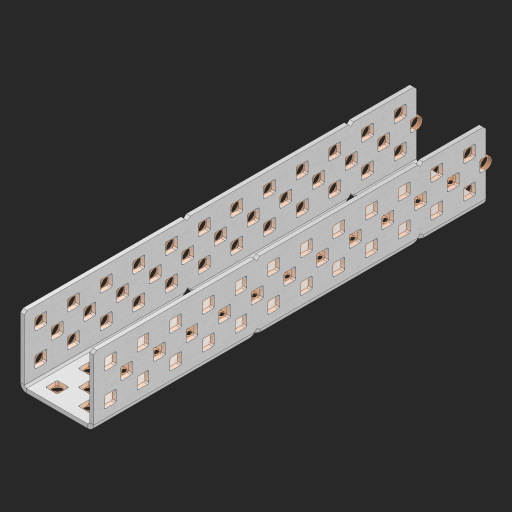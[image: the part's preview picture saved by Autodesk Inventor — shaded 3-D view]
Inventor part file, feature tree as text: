
AUTODESK INVENTOR PART (.ipt)
format: ipt  version: 2023 (Build 270158000, 158)  size: 1,510,912 bytes
history: native  units: in
note: dims shown in document units (in); Inventor stores cm internally (conversion verified against a paired STEP export)
features: other x150, extrude x142, sheet_metal_op x8, sketch x7, mirror x3, pattern_linear x2, chamfer x1
ambient origin geometry x8: Origin, YZ Plane, XZ Plane, XY Plane, X Axis, Y Axis, Z Axis, Center Point
bodies: Solid1 (feature_tree), Body (feature_tree)
feature tree (313):
  sheet_metal_op  "Flanges"
  sheet_metal_op  "Body Pattern"
  pattern_linear  "Center Pattern"  Spacing1=1.0in  [1 undecoded]
  other  "Arc Length"
  mirror  "Notch Mirror"
  pattern_linear  "Notch Pattern"  Spacing1=0.25in  [1 undecoded]
  other  "Diagonal Plane"
  mirror  "Flange 1"
  mirror  "Flange 2"
  chamfer  "End Chamfer"
  sketch  "Sketch1"  dims[d0=1.0in]
  other  "Plate1"
  sketch  "Sketch2"  dims[d1=6.0in]
  other  "Plate2"
  sheet_metal_op  "Bend1"
  sheet_metal_op  "Corner1"
  sketch  "Sketch8"  dims[d2=0.0625in]
  sketch  "Sketch9"  dims[d3=0.0625in]
  other  "Srf91"
  sheet_metal_op  "Body Pattern Sketch"
  other  "Srf92"
  sketch  "Sketch13"  dims[d4=0.0312in]
  sketch  "Sketch15"  dims[d5=0.125in]
  sketch  "Sketch16"  dims[d6=0.0625in d7=1.0in d8=90.0deg d9=0.0312in d10=0.25in d11=0.0625in d12=0.0625in d49=0.182in d50=0.02in d52=0.25in d53=0.0625in d54=0.0in d55=0.172in d56=1.0in d57=0.0in d60=4.7244in d62=0.5in d63=0.7874in d65=0.5in d85=0.1473in d86=0.1782in d88=0.04in d89=0.0625in d90=0.0in d91=0.04in d92=0.0491in d95=2.5in d96=0.04in d97=0.25in d98=45.0deg d99=0.25in d102=2.497in d106=0.182in d107=0.02in d108=0.5in d110=0.0625in d111=0.0in d112=0.172in d113=0.5in d114=0.0in d117=0.5in d118=0.5in d131=0.25in d132=0.25in]
  other  "Srf786"
  other  "Srf889"
  other  "Srf890"
  other  "Srf891"
  other  "Srf892"
  other  "Srf893"
  other  "Srf894"
  other  "Srf895"
  other  "Srf896"
  other  "Srf996"
  other  "Srf997"
  other  "Srf998"
  other  "Srf1315"
  other  "Srf1316"
  other  "Srf1317"
  other  "Srf1325"
  other  "Srf1326"
  other  "Srf1327"
  other  "Srf1328"
  other  "Srf1329"
  other  "Srf1330"
  other  "Srf1331"
  other  "Srf1332"
  other  "Srf1338"
  other  "Srf1339"
  other  "Srf1340"
  other  "Srf1374"
  other  "Srf1375"
  other  "Srf1376"
  other  "Srf1384"
  other  "Srf1385"
  other  "Srf1386"
  other  "Srf1387"
  other  "Srf1388"
  other  "Srf1389"
  other  "Srf1390"
  other  "Srf1391"
  other  "Srf1397"
  other  "Srf1398"
  other  "Srf1399"
  other  "Srf1433"
  other  "Srf1434"
  other  "Srf1473"
  other  "Srf1474"
  other  "Srf1475"
  other  "Srf1476"
  other  "Srf1477"
  other  "Srf1478"
  other  "Srf1479"
  other  "Srf1480"
  other  "Srf1481"
  other  "Srf1482"
  other  "Srf1483"
  other  "Srf1484"
  other  "Srf1500"
  other  "Srf1501"
  other  "Srf1502"
  other  "Srf1503"
  other  "Srf1504"
  other  "Srf1505"
  other  "Srf1506"
  other  "Srf1507"
  other  "Srf1508"
  other  "Srf1509"
  other  "Srf1510"
  other  "Srf1511"
  other  "Srf1512"
  other  "Srf1513"
  other  "Srf1514"
  other  "Srf1515"
  other  "Srf1516"
  other  "Srf1517"
  other  "Srf1518"
  other  "Srf1519"
  other  "Srf1520"
  other  "Srf1521"
  other  "Srf1538"
  other  "Srf1539"
  other  "Srf1540"
  other  "Srf1541"
  other  "Srf1542"
  other  "Srf1543"
  other  "Srf1544"
  other  "Srf1545"
  other  "Srf1546"
  other  "Srf1547"
  other  "Srf1548"
  other  "Srf1549"
  other  "Srf1550"
  other  "Srf1551"
  other  "Srf1552"
  other  "Srf1553"
  other  "Srf1554"
  other  "Srf1555"
  other  "Srf1556"
  other  "Srf1557"
  other  "Srf1558"
  other  "Srf1559"
  other  "Srf1576"
  other  "Srf1577"
  other  "Srf1578"
  other  "Srf1579"
  other  "Srf1580"
  other  "Srf1581"
  other  "Srf1582"
  other  "Srf1583"
  other  "Srf1584"
  other  "Srf1585"
  other  "Srf1586"
  other  "Srf1587"
  other  "Srf1588"
  other  "Srf1589"
  other  "Srf1590"
  other  "Srf1591"
  other  "Srf1592"
  other  "Srf1593"
  other  "Srf1594"
  other  "Srf1595"
  other  "Srf1596"
  other  "Srf1597"
  other  "Srf1614"
  other  "Srf1615"
  other  "Srf1616"
  other  "Srf1617"
  other  "Srf1618"
  other  "Srf1619"
  other  "Srf1620"
  other  "Srf1621"
  other  "Srf1622"
  other  "Srf1623"
  other  "Srf1624"
  other  "Srf1625"
  other  "Srf1626"
  other  "Srf1627"
  other  "Srf1628"
  other  "Srf1629"
  other  "Srf1630"
  other  "Srf1631"
  other  "Srf1632"
  other  "Srf1633"
  other  "Srf1634"
  other  "Srf1635"
  sheet_metal_op  "Body Stamp"
  sheet_metal_op  "Body Circle"
  other  "Center Stamp"
  other  "Center Circle"
  sheet_metal_op  "Notch"
  extrude  "ExtrusionSrf92"  Depth=0.0625in
  extrude  "ExtrusionSrf889"  Depth=0.0625in
  extrude  "ExtrusionSrf890"  Depth=0.182in
  extrude  "ExtrusionSrf891"  Depth=0.02in
  extrude  "ExtrusionSrf892"  Depth=0.25in
  extrude  "ExtrusionSrf893"  Depth=0.0625in
  extrude  "ExtrusionSrf894"  TaperAngle=0.0deg  [1 undecoded]
  extrude  "ExtrusionSrf895"  Depth=0.25in
  extrude  "ExtrusionSrf896"  Depth=1.0in TaperAngle=0.0deg
  extrude  "ExtrusionSrf996"  Depth=0.25in
  extrude  "ExtrusionSrf997"  Depth=0.5in
  extrude  "ExtrusionSrf998"  Depth=0.25in
  extrude  "ExtrusionSrf1315"  Depth=0.25in
  extrude  "ExtrusionSrf1316"  Depth=0.25in
  extrude  "ExtrusionSrf1355"  Depth=0.0625in
  extrude  "ExtrusionSrf1356"  TaperAngle=0.0deg  [1 undecoded]
  extrude  "ExtrusionSrf1357"  Depth=0.25in
  extrude  "ExtrusionSrf1358"  Depth=0.25in
  extrude  "ExtrusionSrf1359"  Depth=2.5in
  extrude  "ExtrusionSrf1360"  Depth=0.25in TaperAngle=45.0deg
  extrude  "ExtrusionSrf1361"  Depth=0.25in
  extrude  "ExtrusionSrf1362"  Depth=0.25in
  extrude  "ExtrusionSrf1363"  Depth=0.182in
  extrude  "ExtrusionSrf1364"  Depth=0.02in
  extrude  "ExtrusionSrf1365"  Depth=0.5in
  extrude  "ExtrusionSrf1366"  Depth=0.0625in
  extrude  "ExtrusionSrf1374"  TaperAngle=0.0deg  [1 undecoded]
  extrude  "ExtrusionSrf1375"  Depth=0.25in
  extrude  "ExtrusionSrf1414"  Depth=0.5in TaperAngle=0.0deg
  extrude  "ExtrusionSrf1415"  Depth=0.5in
  extrude  "ExtrusionSrf1416"  Depth=0.5in
  extrude  "ExtrusionSrf1417"  Depth=0.25in
  extrude  "ExtrusionSrf1418"  Depth=0.25in
  extrude  "ExtrusionSrf1419"  [1 undecoded]
  extrude  "ExtrusionSrf1420"  [1 undecoded]
  extrude  "ExtrusionSrf1421"  [1 undecoded]
  extrude  "ExtrusionSrf1422"  [1 undecoded]
  extrude  "ExtrusionSrf1423"  [1 undecoded]
  extrude  "ExtrusionSrf1424"  [1 undecoded]
  extrude  "ExtrusionSrf1425"  [1 undecoded]
  extrude  "ExtrusionSrf1433"  [1 undecoded]
  extrude  "ExtrusionSrf1434"  [1 undecoded]
  extrude  "ExtrusionSrf1473"  [1 undecoded]
  extrude  "ExtrusionSrf1474"  [1 undecoded]
  extrude  "ExtrusionSrf1475"  [1 undecoded]
  extrude  "ExtrusionSrf1476"  [1 undecoded]
  extrude  "ExtrusionSrf1477"  [1 undecoded]
  extrude  "ExtrusionSrf1478"  [1 undecoded]
  extrude  "ExtrusionSrf1479"  [1 undecoded]
  extrude  "ExtrusionSrf1480"  [1 undecoded]
  extrude  "ExtrusionSrf1481"  [1 undecoded]
  extrude  "ExtrusionSrf1482"  [1 undecoded]
  extrude  "ExtrusionSrf1483"  [1 undecoded]
  extrude  "ExtrusionSrf1484"  [1 undecoded]
  extrude  "ExtrusionSrf1500"  [1 undecoded]
  extrude  "ExtrusionSrf1501"  [1 undecoded]
  extrude  "ExtrusionSrf1502"  [1 undecoded]
  extrude  "ExtrusionSrf1503"  [1 undecoded]
  extrude  "ExtrusionSrf1504"  [1 undecoded]
  extrude  "ExtrusionSrf1505"  [1 undecoded]
  extrude  "ExtrusionSrf1506"  [1 undecoded]
  extrude  "ExtrusionSrf1507"  [1 undecoded]
  extrude  "ExtrusionSrf1508"  [1 undecoded]
  extrude  "ExtrusionSrf1509"  [1 undecoded]
  extrude  "ExtrusionSrf1510"  [1 undecoded]
  extrude  "ExtrusionSrf1511"  [1 undecoded]
  extrude  "ExtrusionSrf1512"  [1 undecoded]
  extrude  "ExtrusionSrf1513"  [1 undecoded]
  extrude  "ExtrusionSrf1514"  [1 undecoded]
  extrude  "ExtrusionSrf1515"  [1 undecoded]
  extrude  "ExtrusionSrf1516"  [1 undecoded]
  extrude  "ExtrusionSrf1517"  [1 undecoded]
  extrude  "ExtrusionSrf1518"  [1 undecoded]
  extrude  "ExtrusionSrf1519"  [1 undecoded]
  extrude  "ExtrusionSrf1520"  [1 undecoded]
  extrude  "ExtrusionSrf1521"  [1 undecoded]
  extrude  "ExtrusionSrf1538"  [1 undecoded]
  extrude  "ExtrusionSrf1539"  [1 undecoded]
  extrude  "ExtrusionSrf1540"  [1 undecoded]
  extrude  "ExtrusionSrf1541"  [1 undecoded]
  extrude  "ExtrusionSrf1542"  [1 undecoded]
  extrude  "ExtrusionSrf1543"  [1 undecoded]
  extrude  "ExtrusionSrf1544"  [1 undecoded]
  extrude  "ExtrusionSrf1545"  [1 undecoded]
  extrude  "ExtrusionSrf1546"  [1 undecoded]
  extrude  "ExtrusionSrf1547"  [1 undecoded]
  extrude  "ExtrusionSrf1548"  [1 undecoded]
  extrude  "ExtrusionSrf1549"  [1 undecoded]
  extrude  "ExtrusionSrf1550"  [1 undecoded]
  extrude  "ExtrusionSrf1551"  [1 undecoded]
  extrude  "ExtrusionSrf1552"  [1 undecoded]
  extrude  "ExtrusionSrf1553"  [1 undecoded]
  extrude  "ExtrusionSrf1554"  [1 undecoded]
  extrude  "ExtrusionSrf1555"  [1 undecoded]
  extrude  "ExtrusionSrf1556"  [1 undecoded]
  extrude  "ExtrusionSrf1557"  [1 undecoded]
  extrude  "ExtrusionSrf1558"  [1 undecoded]
  extrude  "ExtrusionSrf1559"  [1 undecoded]
  extrude  "ExtrusionSrf1576"  [1 undecoded]
  extrude  "ExtrusionSrf1577"  [1 undecoded]
  extrude  "ExtrusionSrf1578"  [1 undecoded]
  extrude  "ExtrusionSrf1579"  [1 undecoded]
  extrude  "ExtrusionSrf1580"  [1 undecoded]
  extrude  "ExtrusionSrf1581"  [1 undecoded]
  extrude  "ExtrusionSrf1582"  [1 undecoded]
  extrude  "ExtrusionSrf1583"  [1 undecoded]
  extrude  "ExtrusionSrf1584"  [1 undecoded]
  extrude  "ExtrusionSrf1585"  [1 undecoded]
  extrude  "ExtrusionSrf1586"  [1 undecoded]
  extrude  "ExtrusionSrf1587"  [1 undecoded]
  extrude  "ExtrusionSrf1588"  [1 undecoded]
  extrude  "ExtrusionSrf1589"  [1 undecoded]
  extrude  "ExtrusionSrf1590"  [1 undecoded]
  extrude  "ExtrusionSrf1591"  [1 undecoded]
  extrude  "ExtrusionSrf1592"  [1 undecoded]
  extrude  "ExtrusionSrf1593"  [1 undecoded]
  extrude  "ExtrusionSrf1594"  [1 undecoded]
  extrude  "ExtrusionSrf1595"  [1 undecoded]
  extrude  "ExtrusionSrf1596"  [1 undecoded]
  extrude  "ExtrusionSrf1597"  [1 undecoded]
  extrude  "ExtrusionSrf1614"  [1 undecoded]
  extrude  "ExtrusionSrf1615"  [1 undecoded]
  extrude  "ExtrusionSrf1616"  [1 undecoded]
  extrude  "ExtrusionSrf1617"  [1 undecoded]
  extrude  "ExtrusionSrf1618"  [1 undecoded]
  extrude  "ExtrusionSrf1619"  [1 undecoded]
  extrude  "ExtrusionSrf1620"  [1 undecoded]
  extrude  "ExtrusionSrf1621"  [1 undecoded]
  extrude  "ExtrusionSrf1622"  [1 undecoded]
  extrude  "ExtrusionSrf1623"  [1 undecoded]
  extrude  "ExtrusionSrf1624"  [1 undecoded]
  extrude  "ExtrusionSrf1625"  [1 undecoded]
  extrude  "ExtrusionSrf1626"  [1 undecoded]
  extrude  "ExtrusionSrf1627"  [1 undecoded]
  extrude  "ExtrusionSrf1628"  [1 undecoded]
  extrude  "ExtrusionSrf1629"  [1 undecoded]
  extrude  "ExtrusionSrf1630"  [1 undecoded]
  extrude  "ExtrusionSrf1631"  [1 undecoded]
  extrude  "ExtrusionSrf1632"  [1 undecoded]
  extrude  "ExtrusionSrf1633"  [1 undecoded]
  extrude  "ExtrusionSrf1634"  [1 undecoded]
  extrude  "ExtrusionSrf1635"  [1 undecoded]
note: 114 required parameter values undecoded (feature->parameter linkage not recoverable at this tier; creation-order binding heuristic only, values carry confidence <= 0.55)
